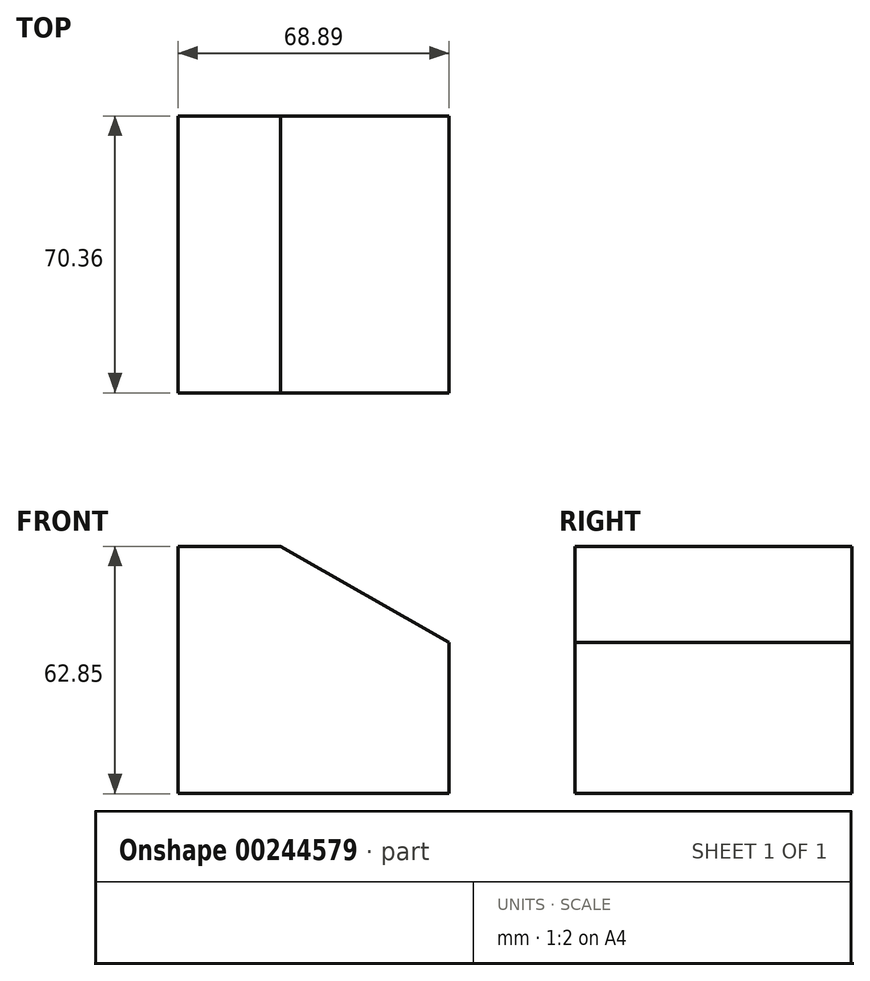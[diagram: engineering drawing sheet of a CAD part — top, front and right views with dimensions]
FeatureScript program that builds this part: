
annotation { "Feature Type Name" : "Feature", "Feature Type Description" : "" }
export const myFeature = defineFeature(function(context is Context, id is Id, definition is map)
    precondition{}
    {
        {
            var Q0;
            Q0=qCreatedBy(makeId("Front.planeOp"),FACE);
            var sketch = newSketch(context, id + "F0", { "sketchPlane" : qUnion([Q0])});
            skLineSegment(sketch, "E0.bottom", {"start": v(-55.1, 34.33) * mm, "end": v(13.8, 34.33) * mm});
            skLineSegment(sketch, "E0.top", {"start": v(-55.1, -28.52) * mm, "end": v(13.8, -28.52) * mm});
            skLineSegment(sketch, "E0.left", {"start": v(-55.1, 34.33) * mm, "end": v(-55.1, -28.52) * mm});
            skLineSegment(sketch, "E0.right", {"start": v(13.8, 34.33) * mm, "end": v(13.8, -28.52) * mm});
            skSolve(sketch);
        }
        {
            var Q0;
            Q0=makeQuery(id+"F0.imprint","IMPRINT",FACE,{"disambiguationData":[TD([[makeQuery(id+"F0.imprint","IMPRINT",EDGE,{"derivedFrom":sQuery(id+"F0.wireOp",EDGE,"E0.bottom")}),-1.0]])]});
            extrude(context, id + "F1", {"entities" : qUnion([Q0]), "depth" : 70.36 * mm});
        }
        {
            var Q0;
            Q0=makeQuery(id+"F1.opExtrude","CAP_FACE",FACE,{"disambiguationData":[OSD([sQuery(id+"F0.wireOp",EDGE,"E0.bottom"),sQuery(id+"F0.wireOp",EDGE,"E0.top"),sQuery(id+"F0.wireOp",EDGE,"E0.left"),sQuery(id+"F0.wireOp",EDGE,"E0.right")])],"isStart":false});
            var sketch = newSketch(context, id + "F2", { "sketchPlane" : qUnion([Q0])});
            skLineSegment(sketch, "E1", {"start": v(-29.08, 34.33) * mm, "end": v(13.8, 9.85) * mm});
            skLineSegment(sketch, "E2", {"start": v(-29.08, 34.33) * mm, "end": v(13.8, 34.33) * mm});
            skLineSegment(sketch, "E3", {"start": v(13.8, 34.33) * mm, "end": v(13.8, 9.85) * mm});
            skSolve(sketch);
        }
        {
            var Q0;
            Q0=makeQuery(id+"F2.imprint","IMPRINT",FACE,{"disambiguationData":[TD([[makeQuery(id+"F2.imprint","IMPRINT",EDGE,{"derivedFrom":sQuery(id+"F2.wireOp",EDGE,"E1")}),1.0]])]});
            extrude(context, id + "F3", {"entities" : qUnion([Q0]), "operationType" : NewBodyOperationType.REMOVE, "endBound" : BoundingType.THROUGH_ALL, "oppositeDirection" : true, "depth" : 25.4 * mm});
        }
    });
